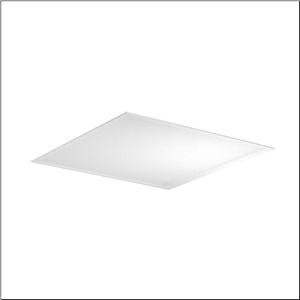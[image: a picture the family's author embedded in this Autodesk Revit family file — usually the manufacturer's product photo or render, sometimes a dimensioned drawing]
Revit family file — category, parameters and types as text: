
# Revit family: apollon_r__31_square_51mp12wd2m42_b676
name_source: partatom
category: Lighting Fixtures
units: mm (PartAtom-declared; Revit-internal decimal feet)

## family parameters
Cut with Voids When Loaded = No
Host = Face
Light Source = No
Part Type = Normal
Room Calculation Point = No
Round Connector Dimension = Use Diameter
Shared = No

## types (1)
- --- (1 x LED, 4000 lm, 27.5 W, 4000K)
    Apparent Load = 28 VA
    CIE Flux Codes = 62 87 97 100 100
    Color Rendering = 80
    Color Temperature = 4000K
    Default Elevation = 1800 mm
    Description = Apollon® 31 square, office luminaire, primary optical cover: micro prismatic cover, of PMMA, CAT 2 (L<= 3000cd/m²), light emission: direct distribution, primary light characteristic: symmetric, installation type: lay-in mounting, LED, rated luminous flux: 4.000lm, luminous efficacy: 142lm/W, light colour: 830/840, colour temperature: 3000/4000K, with terminal, 5-pole, mains connection: 220..240V, AC/DC, 0/50..60Hz, rated input power: 28W, housing, of aluminium, traffic white (RAL 9016), module: M600, length: 595mm, width: 595mm, height: 32mm, housing upper side, of sheet steel, galvanised, protection rating (complete): IP20, protection rating (on room side): IP40, insulation class (complete): insulation class II (safety insulation), certification: CE, ENEC, impact resistance: IK03, permissible operating ambient temperature: -20..+40°C, permissible storage temperature: -20..+60°C, packaging unit: 1 piece
    Height = 0 mm  [stored 0 ft]
    Lamp = 1 x LED
    Lamp Light Flux = 4000 lm
    Lamp Power = 27.5 W
    Lamp count = 1
    Length = 595 mm
    Luminous efficacy = 145 lm/W
    Manufacturer = Siteco
    ModVariant = No
    Model = 51MP12WD2M42
    Mounting Place = Ceiling
    Mounting Type = Recessed
    Number of Poles = 1
    OnlyDefault = Yes
    Power Factor = 1
    Product Name = Apollon® 31 square
    Product group = office luminaire | ceiling recessed
    ProductGroupID = 400
    Protection Class = Protection class II
    Protection Degree = IP 20
    RLX_Detail_Level = 1
    RLX_Emergency_Light_Flux = 0 lm
    RLX_Emergency_Type = 0
    RLX_Emergency_Type_DB = No
    RlxData = <blob elided: 12729 chars, md5=cbfb8486>
    Socket = socket
    Standby Power = 0 W
    System Light Flux = 4000 lm
    System Power = 28 W
    Type Comments = factory setting: colour temperature 4000K
    Type Image = l_1291035.jpg
    URL = http://relux.com
    VarID = @adj_045639
    Voltage = 0 V
    Weight = 0.00 kg
    Width = 595 mm

note: [stored X ft] marks values corroborated as IEEE doubles in the binary element streams (Revit-internal decimal feet)

## geometry (parser evidence)
native form markers: Sweep x11
no freeform markers — native parametric forms only
